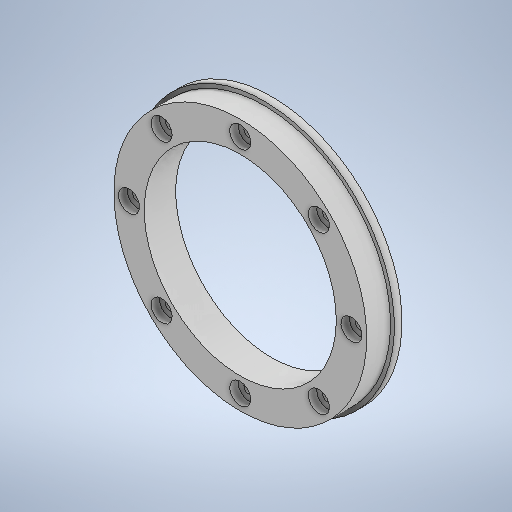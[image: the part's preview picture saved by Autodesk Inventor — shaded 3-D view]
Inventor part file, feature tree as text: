
AUTODESK INVENTOR PART (.ipt)
format: ipt  version: 2025 (Build 290162010, 162A)  size: 332,288 bytes
history: native  units: mm
features: extrude x4, sketch x4, pattern_circular x1, projected_geometry x1
ambient origin geometry x8: Origin, YZ Plane, XZ Plane, XY Plane, X Axis, Y Axis, Z Axis, Center Point
bodies: Solid1 (feature_tree)
feature tree (10):
  extrude  "Extrusion1"  Depth=250.0mm
  extrude  "Extrusion2"  Depth=41.0mm
  extrude  "Extrusion3"  Depth=80.0mm TaperAngle=360.0deg
  pattern_circular  "Circular Pattern1"  [2 undecoded]
  extrude  "Extrusion4"  Depth=10.0mm
  sketch  "Sketch1"  dims[d0=39.5mm d1=250.0mm]
  sketch  "Sketch2"  dims[d2=41.0mm d3=0.0mm d4=12.5mm]
  projected_geometry  "Projected Loop1"
  sketch  "Sketch3"  dims[d5=0.0mm d6=0.0mm d7=80.0mm d8=360.0deg]
  sketch  "Sketch4"  dims[d10=27.5mm d11=11.0mm d12=0.0mm d13=5.0mm d14=10.0mm d15=0.0mm]
note: 2 required parameter values undecoded (feature->parameter linkage not recoverable at this tier; creation-order binding heuristic only, values carry confidence <= 0.55)
